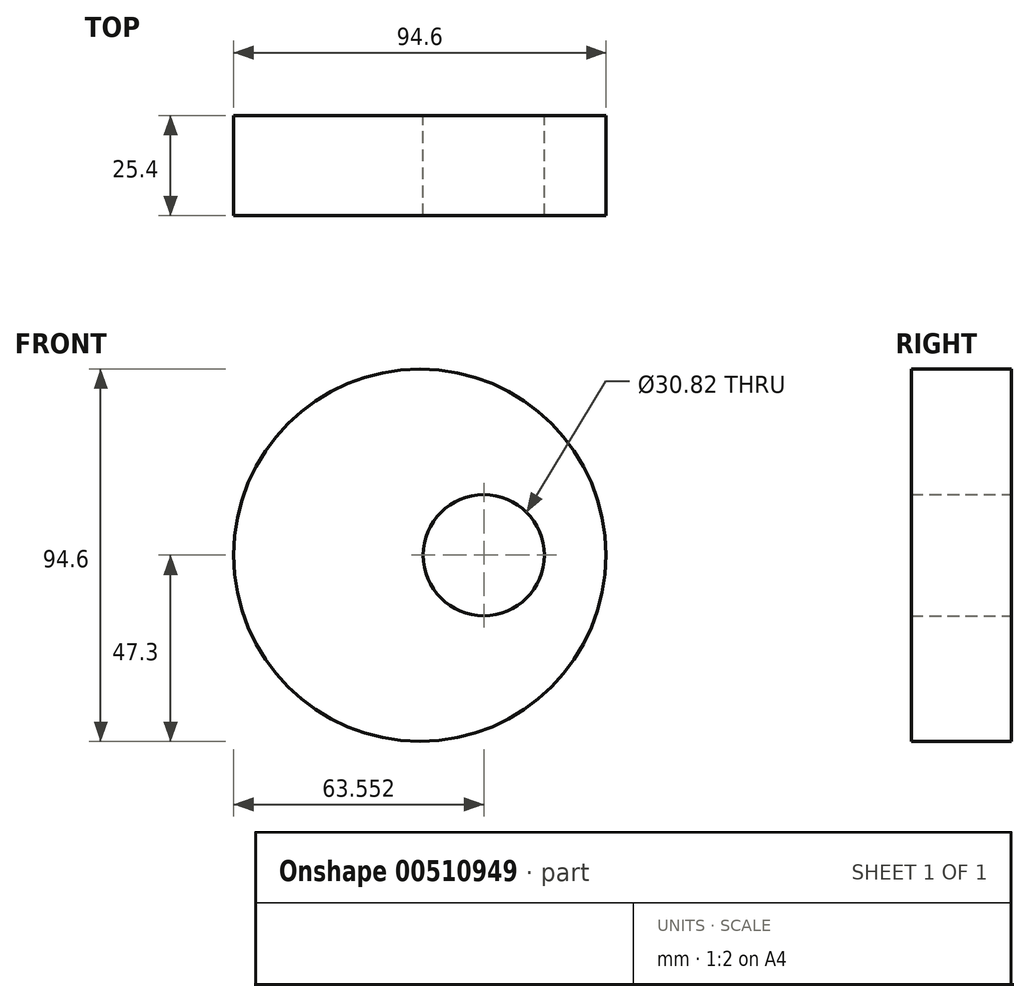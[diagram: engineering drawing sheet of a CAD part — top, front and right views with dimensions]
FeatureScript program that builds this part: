
annotation { "Feature Type Name" : "Feature", "Feature Type Description" : "" }
export const myFeature = defineFeature(function(context is Context, id is Id, definition is map)
    precondition{}
    {
        {
            var Q0;
            Q0=qCreatedBy(makeId("Front.planeOp"),FACE);
            var sketch = newSketch(context, id + "F0", { "sketchPlane" : qUnion([Q0])});
            skCircle(sketch, "E0", {"center": v(0, 0) * mm, "radius": 47.3 * mm});
            skCircle(sketch, "E1", {"center": v(16.25, 0) * mm, "radius": 15.41 * mm});
            skSolve(sketch);
        }
        {
            var Q0;
            Q0 = qSketchRegion(id + "F0", true);
            extrude(context, id + "F1", {"entities" : qUnion([Q0]), "endBound" : BoundingType.SYMMETRIC, "depth" : 25.4 * mm});
        }
    });
